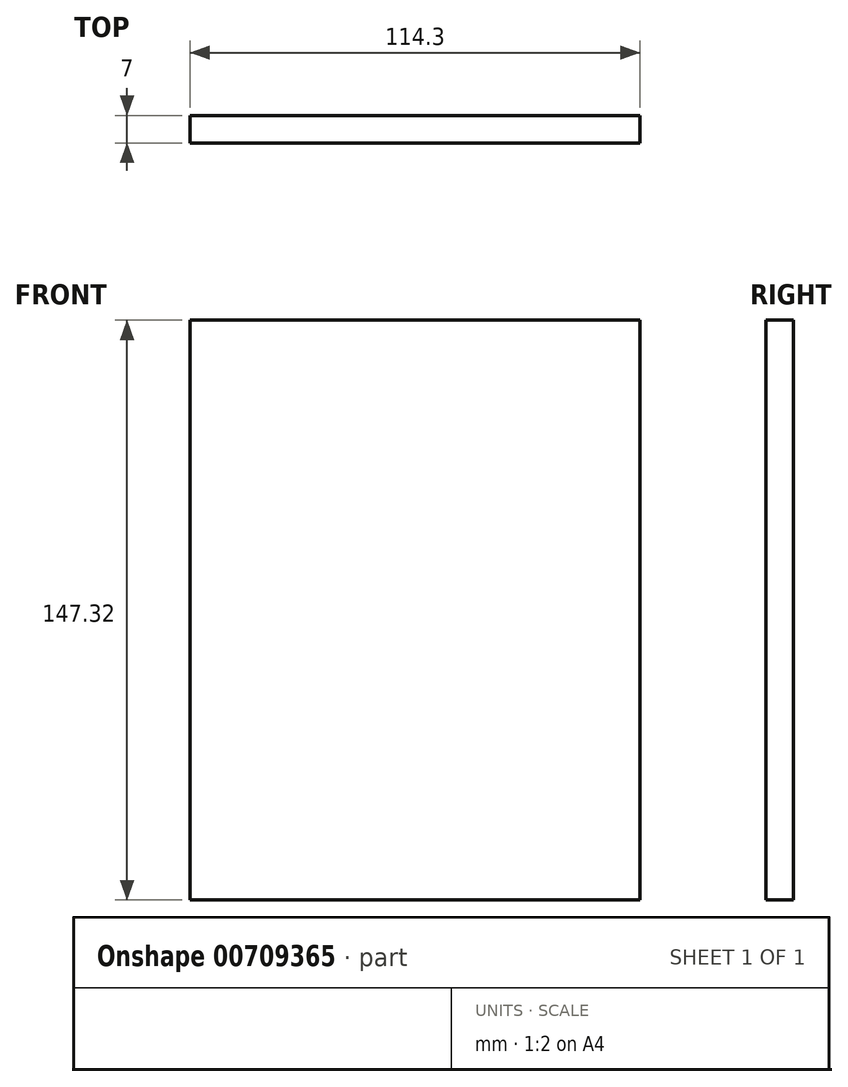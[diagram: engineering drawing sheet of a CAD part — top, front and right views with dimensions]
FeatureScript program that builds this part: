
annotation { "Feature Type Name" : "Feature", "Feature Type Description" : "" }
export const myFeature = defineFeature(function(context is Context, id is Id, definition is map)
    precondition{}
    {
        {
            var Q0;
            Q0=qCreatedBy(makeId("Front.planeOp"),FACE);
            var sketch = newSketch(context, id + "F0", { "sketchPlane" : qUnion([Q0])});
            skLineSegment(sketch, "E0.bottom", {"start": v(-63.52, 125.36) * mm, "end": v(50.78, 125.36) * mm});
            skLineSegment(sketch, "E0.top", {"start": v(-63.52, -21.96) * mm, "end": v(50.78, -21.96) * mm});
            skLineSegment(sketch, "E0.left", {"start": v(-63.52, 125.36) * mm, "end": v(-63.52, -21.96) * mm});
            skLineSegment(sketch, "E0.right", {"start": v(50.78, 125.36) * mm, "end": v(50.78, -21.96) * mm});
            skSolve(sketch);
        }
        {
            var Q0;
            Q0 = qSketchRegion(id + "F0", true);
            extrude(context, id + "F1", {"entities" : qUnion([Q0]), "depth" : 7 * mm, "offsetDistance" : 25.4 * mm});
        }
    });
